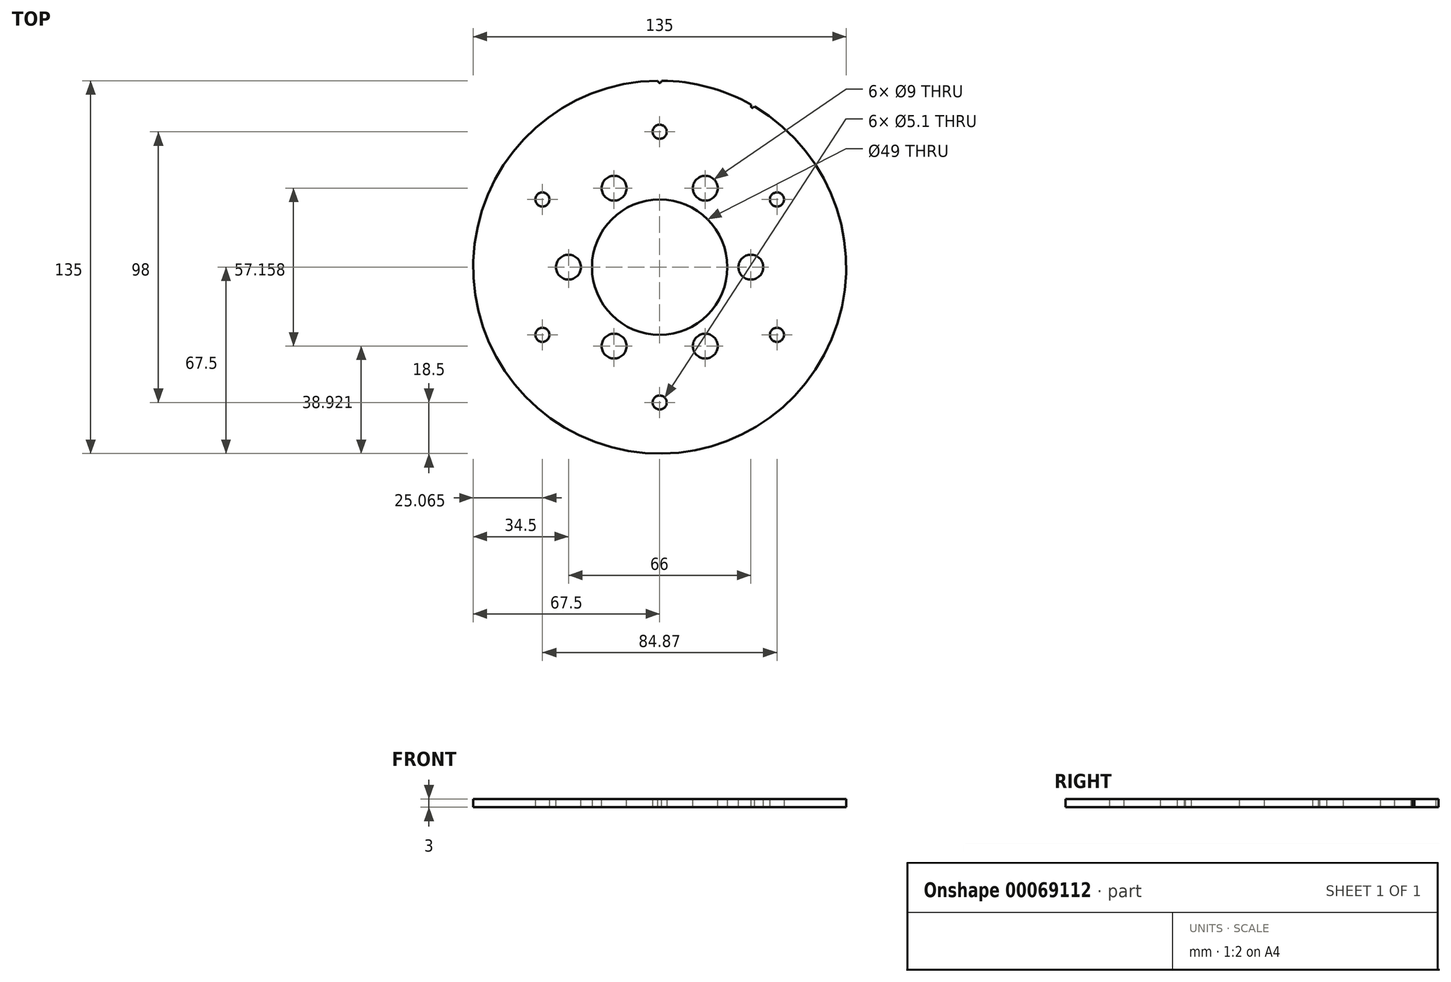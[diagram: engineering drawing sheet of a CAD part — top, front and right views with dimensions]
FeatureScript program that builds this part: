
annotation { "Feature Type Name" : "Feature", "Feature Type Description" : "" }
export const myFeature = defineFeature(function(context is Context, id is Id, definition is map)
    precondition{}
    {
        {
            var Q0;
            Q0=qCreatedBy(makeId("Top.planeOp"),FACE);
            var sketch = newSketch(context, id + "F0", { "sketchPlane" : qUnion([Q0])});
            skCircle(sketch, "E0", {"center": v(0, 0) * mm, "radius": 67.5 * mm});
            skCircle(sketch, "E1", {"center": v(0, 0) * mm, "radius": 49 * mm, "construction": true});
            skCircle(sketch, "E2", {"center": v(0, 0) * mm, "radius": 24.5 * mm});
            skLineSegment(sketch, "E3", {"start": v(0, 0) * mm, "end": v(0, 49) * mm, "construction": true});
            skCircle(sketch, "E4", {"center": v(0, 49) * mm, "radius": 2.55 * mm});
            skSolve(sketch);
        }
        {
            var Q0;
            {var subQ2=sQuery(id+"F0.wireOp",EDGE,"E0");Q0=makeQuery(id+"F0.imprint","IMPRINT",FACE,{"disambiguationData":[TD([[makeQuery(id+"F0.imprint","IMPRINT",EDGE,{"derivedFrom":subQ2}),-1.0]])]});}
            var Q1;
            Q1=makeQuery(id+"F0.imprint","IMPRINT",FACE,{"disambiguationData":[TD([[makeQuery(id+"F0.imprint","IMPRINT",EDGE,{"derivedFrom":sQuery(id+"F0.wireOp",EDGE,"E0")}),1.0]])]});
            extrude(context, id + "F1", {"entities" : qUnion([Q0, Q1]), "depth" : 3 * mm});
        }
        {
            var Q0;
            Q0=makeQuery(id+"F1.opExtrude","SWEPT_FACE",FACE,{"disambiguationData":[OSD([sQuery(id+"F0.wireOp",EDGE,"E4")])]});
            var Q1;
            Q1=makeQuery(id+"F1.opExtrude","CAP_EDGE",EDGE,{"disambiguationData":[OSD([sQuery(id+"F0.wireOp",EDGE,"E2")])],"isStart":true});
            circularPattern(context, id + "F2", {"faces" : qUnion([Q0]), "axis" : qUnion([Q1]), "angle" : 360 * degree, "instanceCount" : round(6), "equalSpace" : true, "patternType" : PatternType.FACE});
        }
        {
            var Q0;
            Q0=makeQuery(id+"F1.opExtrude","CAP_FACE",FACE,{"disambiguationData":[OSD([sQuery(id+"F0.wireOp",EDGE,"E0"),sQuery(id+"F0.wireOp",EDGE,"E2"),sQuery(id+"F0.wireOp",EDGE,"E4")])],"isStart":false});
            var sketch = newSketch(context, id + "F3", { "sketchPlane" : qUnion([Q0])});
            skCircle(sketch, "E5", {"center": v(0, 0) * mm, "radius": 66 * mm, "construction": true});
            skArc(sketch, "E6", {"start": v(0.7, 67.5) * mm, "mid": v(0, 67.5) * mm, "end": v(-0.7, 67.5) * mm});
            skLineSegment(sketch, "E7", {"start": v(0, 0) * mm, "end": v(0, 66) * mm, "construction": true});
            skLineSegment(sketch, "E8", {"start": v(0, 66) * mm, "end": v(-0.7, 67.5) * mm});
            skLineSegment(sketch, "E9", {"start": v(0, 66) * mm, "end": v(0.7, 67.5) * mm});
            skLineSegment(sketch, "E10", {"start": v(0, 0) * mm, "end": v(33, 57.16) * mm, "construction": true});
            skLineSegment(sketch, "E11", {"start": v(33, 57.16) * mm, "end": v(33.14, 58.8) * mm});
            skLineSegment(sketch, "E12", {"start": v(33, 57.16) * mm, "end": v(34.35, 58.1) * mm});
            skSolve(sketch);
        }
        {
            var Q0;
            Q0=makeQuery(id+"F3.imprint","IMPRINT",FACE,{"disambiguationData":[TD([[makeQuery(id+"F3.imprint","IMPRINT",EDGE,{"derivedFrom":sQuery(id+"F3.wireOp",EDGE,"E6")}),1.0]])]});
            var Q1;
            Q1=makeQuery(id+"F3.imprint","IMPRINT",FACE,{"disambiguationData":[TD([[makeQuery(id+"F3.imprint","IMPRINT",EDGE,{"derivedFrom":sQuery(id+"F3.wireOp",EDGE,"77b4c7fe-b791-4ae9-81ec-833696c1d917")}),-1.0]])]});
            var Q2;
            Q2=makeQuery(id+"F3.imprint","IMPRINT",FACE,{"disambiguationData":[TD([[makeQuery(id+"F3.imprint","IMPRINT",EDGE,{"derivedFrom":sQuery(id+"F3.wireOp",EDGE,"a08668e5-94e9-44ca-8fdd-dda859cc1fb0")}),-1.0]])]});
            var Q3;
            Q3=makeQuery(id+"F3.imprint","IMPRINT",FACE,{"disambiguationData":[TD([[makeQuery(id+"F3.imprint","IMPRINT",EDGE,{"derivedFrom":sQuery(id+"F3.wireOp",EDGE,"E11")}),-1.0]])]});
            extrude(context, id + "F4", {"entities" : qUnion([Q0, Q1, Q2, Q3]), "operationType" : NewBodyOperationType.REMOVE, "endBound" : BoundingType.THROUGH_ALL, "oppositeDirection" : true, "depth" : 25 * mm, "offsetDistance" : 25 * mm});
        }
        {
            var Q0;
            Q0=makeQuery(id+"F4.boolean.opBoolean","COPY",EDGE,{"derivedFrom":makeQuery(id+"F4.opExtrude","SWEPT_EDGE",EDGE,{"disambiguationData":[OSD([sQuery(id+"F3.wireOp",EDGE,"E8"),sQuery(id+"F3.wireOp",EDGE,"E9")])]})});
            var Q1;
            Q1=makeQuery(id+"F4.boolean.opBoolean","COPY",EDGE,{"derivedFrom":makeQuery(id+"F4.opExtrude","SWEPT_EDGE",EDGE,{"disambiguationData":[OSD([sQuery(id+"F3.wireOp",EDGE,"77b4c7fe-b791-4ae9-81ec-833696c1d917"),sQuery(id+"F3.wireOp",EDGE,"b0c6beb3-5203-4bea-b8da-ac0edfaee701")])]})});
            var Q2;
            Q2=makeQuery(id+"F4.boolean.opBoolean","COPY",EDGE,{"derivedFrom":makeQuery(id+"F4.opExtrude","SWEPT_EDGE",EDGE,{"disambiguationData":[OSD([sQuery(id+"F3.wireOp",EDGE,"a08668e5-94e9-44ca-8fdd-dda859cc1fb0"),sQuery(id+"F3.wireOp",EDGE,"60cfae09-5c82-4859-ab49-940020c40963")])]})});
            var Q3;
            Q3=makeQuery(id+"F4.boolean.opBoolean","COPY",EDGE,{"derivedFrom":makeQuery(id+"F4.opExtrude","SWEPT_EDGE",EDGE,{"disambiguationData":[OSD([sQuery(id+"F3.wireOp",EDGE,"E11"),sQuery(id+"F3.wireOp",EDGE,"E12")])]})});
            fillet(context, id + "F5", {"entities" : qUnion([Q0, Q1, Q2, Q3]), "radius" : 0.5 * mm, "tangentPropagation" : true, "allowEdgeOverflow" : false});
        }
        {
            var Q0;
            Q0=makeQuery(id+"F1.opExtrude","CAP_FACE",FACE,{"disambiguationData":[OSD([sQuery(id+"F0.wireOp",EDGE,"E0"),sQuery(id+"F0.wireOp",EDGE,"E2"),sQuery(id+"F0.wireOp",EDGE,"E4")])],"isStart":false});
            var sketch = newSketch(context, id + "F6", { "sketchPlane" : qUnion([Q0])});
            skLineSegment(sketch, "E13", {"start": v(0, 0) * mm, "end": v(-33.75, 58.46) * mm, "construction": true});
            skCircle(sketch, "E14", {"center": v(-16.5, 28.58) * mm, "radius": 4.5 * mm});
            skSolve(sketch);
        }
        {
            var Q0;
            Q0 = qSketchRegion(id + "F6", true);
            extrude(context, id + "F7", {"entities" : qUnion([Q0]), "operationType" : NewBodyOperationType.REMOVE, "endBound" : BoundingType.UP_TO_NEXT, "oppositeDirection" : true, "depth" : 25 * mm, "offsetDistance" : 25 * mm});
        }
        {
            var Q0;
            Q0=makeQuery(id+"F7.boolean.opBoolean","COPY",FACE,{"derivedFrom":makeQuery(id+"F7.opExtrude","SWEPT_FACE",FACE,{"disambiguationData":[OSD([sQuery(id+"F6.wireOp",EDGE,"E14")])]})});
            var Q1;
            Q1=makeQuery(id+"F1.opExtrude","CAP_EDGE",EDGE,{"disambiguationData":[OSD([sQuery(id+"F0.wireOp",EDGE,"E2")])],"isStart":false});
            circularPattern(context, id + "F8", {"patternType" : PatternType.FACE, "faces" : qUnion([Q0]), "axis" : qUnion([Q1]), "angle" : 360 * degree, "instanceCount" : 6, "equalSpace" : true});
        }
    });
